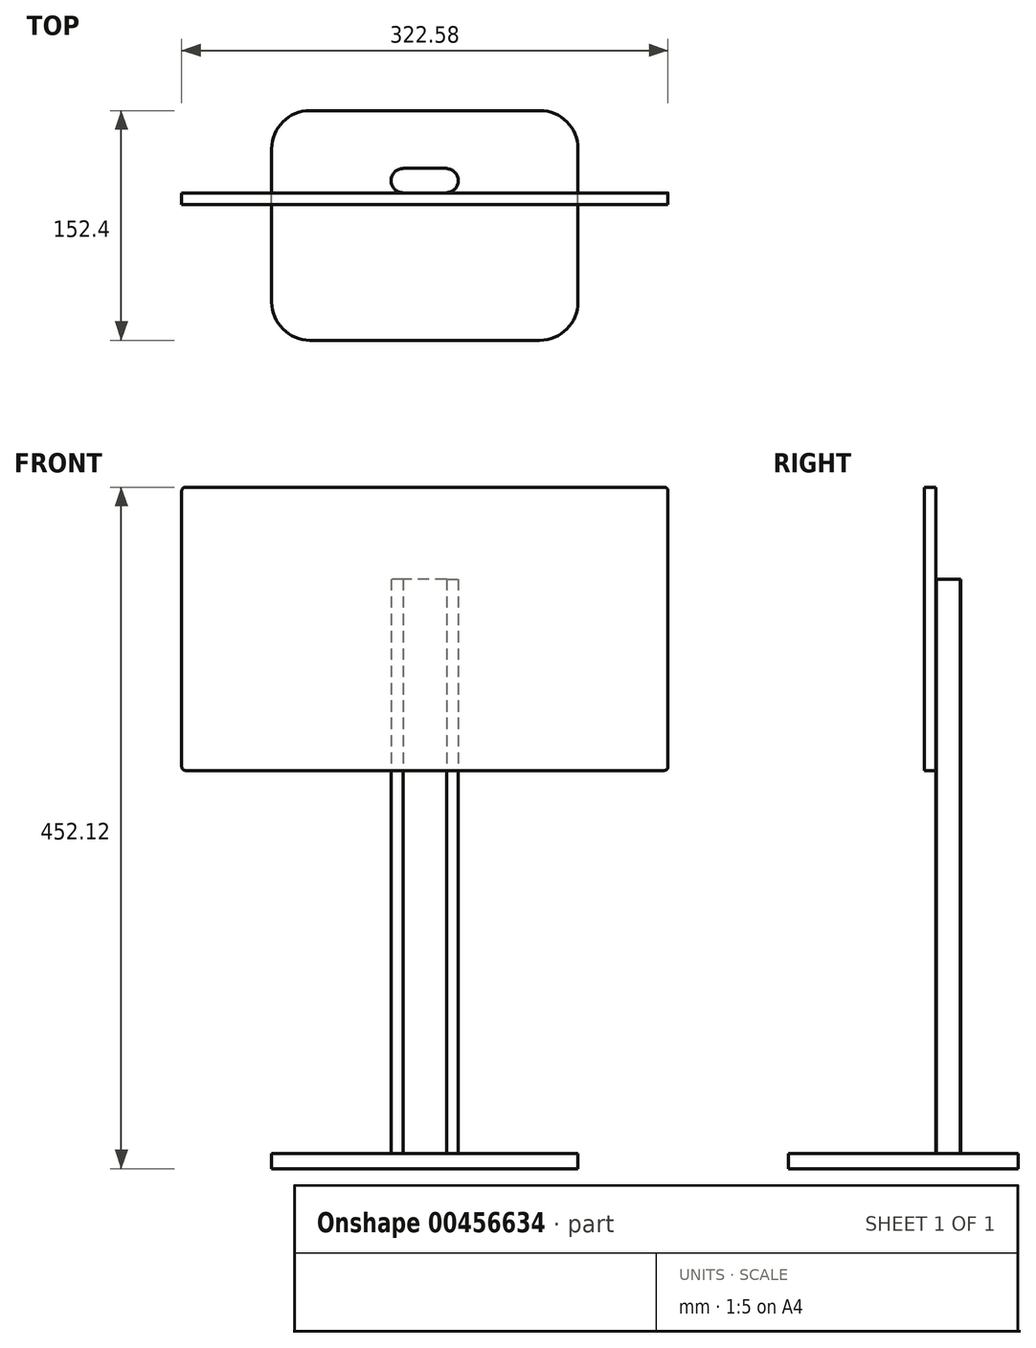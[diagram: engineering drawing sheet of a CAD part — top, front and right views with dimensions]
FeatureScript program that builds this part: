
annotation { "Feature Type Name" : "Feature", "Feature Type Description" : "" }
export const myFeature = defineFeature(function(context is Context, id is Id, definition is map)
    precondition{}
    {
        {
            var Q0;
            Q0=qCreatedBy(makeId("Top.planeOp"),FACE);
            var sketch = newSketch(context, id + "F0", { "sketchPlane" : qUnion([Q0])});
            skLineSegment(sketch, "E0.bottom", {"start": v(76.2, -76.2) * mm, "end": v(-76.2, -76.2) * mm});
            skLineSegment(sketch, "E0.top", {"start": v(76.2, 76.2) * mm, "end": v(-76.2, 76.2) * mm});
            skLineSegment(sketch, "E0.left", {"start": v(101.6, -50.8) * mm, "end": v(101.6, 50.8) * mm});
            skLineSegment(sketch, "E0.right", {"start": v(-101.6, -50.8) * mm, "end": v(-101.6, 50.8) * mm});
            skPoint(sketch, "E0.middle", {"position": v(0, 0) * mm});
            skPoint(sketch, "E1.visualSharp", {"position": v(-101.6, 76.2) * mm});
            skArc(sketch, "E1.filletArc", {"start": v(-76.2, 76.2) * mm, "mid": v(-94.16, 68.76) * mm, "end": v(-101.6, 50.8) * mm});
            skPoint(sketch, "E2.visualSharp", {"position": v(-101.6, -76.2) * mm});
            skArc(sketch, "E2.filletArc", {"start": v(-101.6, -50.8) * mm, "mid": v(-94.16, -68.76) * mm, "end": v(-76.2, -76.2) * mm});
            skPoint(sketch, "E3.visualSharp", {"position": v(101.6, -76.2) * mm});
            skArc(sketch, "E3.filletArc", {"start": v(76.2, -76.2) * mm, "mid": v(94.16, -68.76) * mm, "end": v(101.6, -50.8) * mm});
            skPoint(sketch, "E4.visualSharp", {"position": v(101.6, 76.2) * mm});
            skArc(sketch, "E4.filletArc", {"start": v(101.6, 50.8) * mm, "mid": v(94.16, 68.76) * mm, "end": v(76.2, 76.2) * mm});
            skSolve(sketch);
        }
        {
            var Q0;
            Q0 = qSketchRegion(id + "F0", true);
            extrude(context, id + "F1", {"entities" : qUnion([Q0]), "oppositeDirection" : true, "depth" : 10.16 * mm});
        }
        {
            var Q0;
            Q0=makeQuery(id+"F1.opExtrude","CAP_FACE",FACE,{"disambiguationData":[OSD([sQuery(id+"F0.wireOp",EDGE,"E0.bottom"),sQuery(id+"F0.wireOp",EDGE,"E0.top"),sQuery(id+"F0.wireOp",EDGE,"E0.left"),sQuery(id+"F0.wireOp",EDGE,"E0.right"),sQuery(id+"F0.wireOp",EDGE,"E1.filletArc"),sQuery(id+"F0.wireOp",EDGE,"E2.filletArc"),sQuery(id+"F0.wireOp",EDGE,"E3.filletArc"),sQuery(id+"F0.wireOp",EDGE,"E4.filletArc")])],"isStart":true});
            var sketch = newSketch(context, id + "F2", { "sketchPlane" : qUnion([Q0])});
            skLineSegment(sketch, "E5.bottom", {"start": v(14.32, 21.46) * mm, "end": v(-14.32, 21.46) * mm});
            skLineSegment(sketch, "E5.top", {"start": v(14.32, 37.9) * mm, "end": v(-14.32, 37.9) * mm});
            skLineSegment(sketch, "E5.left", {"start": v(14.32, 21.46) * mm, "end": v(14.32, 37.9) * mm});
            skLineSegment(sketch, "E5.right", {"start": v(-14.32, 21.46) * mm, "end": v(-14.32, 37.9) * mm});
            skPoint(sketch, "E5.middle", {"position": v(0, 29.68) * mm});
            skCircle(sketch, "E6", {"center": v(-14.32, 29.68) * mm, "radius": 8.1 * mm});
            skCircle(sketch, "E7", {"center": v(14.32, 29.68) * mm, "radius": 7.86 * mm});
            skSolve(sketch);
        }
        {
            var Q0;
            Q0 = qSketchRegion(id + "F2", true);
            extrude(context, id + "F3", {"entities" : qUnion([Q0]), "operationType" : NewBodyOperationType.ADD, "depth" : 381 * mm});
        }
        {
            var Q0;
            Q0=makeQuery(id+"F3.opExtrude","SWEPT_FACE",FACE,{"disambiguationData":[OSD([sQuery(id+"F2.wireOp",EDGE,"E5.bottom")])]});
            var sketch = newSketch(context, id + "F4", { "sketchPlane" : qUnion([Q0])});
            skLineSegment(sketch, "E8.bottom", {"start": v(158.75, 254) * mm, "end": v(-158.75, 254) * mm});
            skLineSegment(sketch, "E8.top", {"start": v(158.75, 441.96) * mm, "end": v(-158.75, 441.96) * mm});
            skLineSegment(sketch, "E8.left", {"start": v(161.29, 256.54) * mm, "end": v(161.3, 439.42) * mm});
            skLineSegment(sketch, "E8.right", {"start": v(-161.3, 256.54) * mm, "end": v(-161.29, 439.42) * mm});
            skPoint(sketch, "E8.middle", {"position": v(0, 347.98) * mm});
            skPoint(sketch, "E8.middle.positionSnap0", {"position": v(0, 381) * mm});
            skPoint(sketch, "E8.centerSnap0", {"position": v(0, 381) * mm});
            skPoint(sketch, "E9.visualSharp", {"position": v(-161.29, 441.96) * mm});
            skArc(sketch, "E9.filletArc", {"start": v(-158.75, 441.96) * mm, "mid": v(-160.55, 441.22) * mm, "end": v(-161.29, 439.42) * mm});
            skPoint(sketch, "E10.visualSharp", {"position": v(161.3, 441.96) * mm});
            skArc(sketch, "E10.filletArc", {"start": v(161.3, 439.42) * mm, "mid": v(160.55, 441.22) * mm, "end": v(158.75, 441.96) * mm});
            skPoint(sketch, "E11.visualSharp", {"position": v(161.29, 254) * mm});
            skArc(sketch, "E11.filletArc", {"start": v(158.75, 254) * mm, "mid": v(160.55, 254.74) * mm, "end": v(161.29, 256.54) * mm});
            skPoint(sketch, "E12.visualSharp", {"position": v(-161.3, 254) * mm});
            skArc(sketch, "E12.filletArc", {"start": v(-161.29, 256.54) * mm, "mid": v(-160.55, 254.74) * mm, "end": v(-158.75, 254) * mm});
            skSolve(sketch);
        }
        {
            var Q0;
            Q0 = qSketchRegion(id + "F4", true);
            extrude(context, id + "F5", {"entities" : qUnion([Q0]), "operationType" : NewBodyOperationType.ADD, "depth" : 7.62 * mm});
        }
    });
